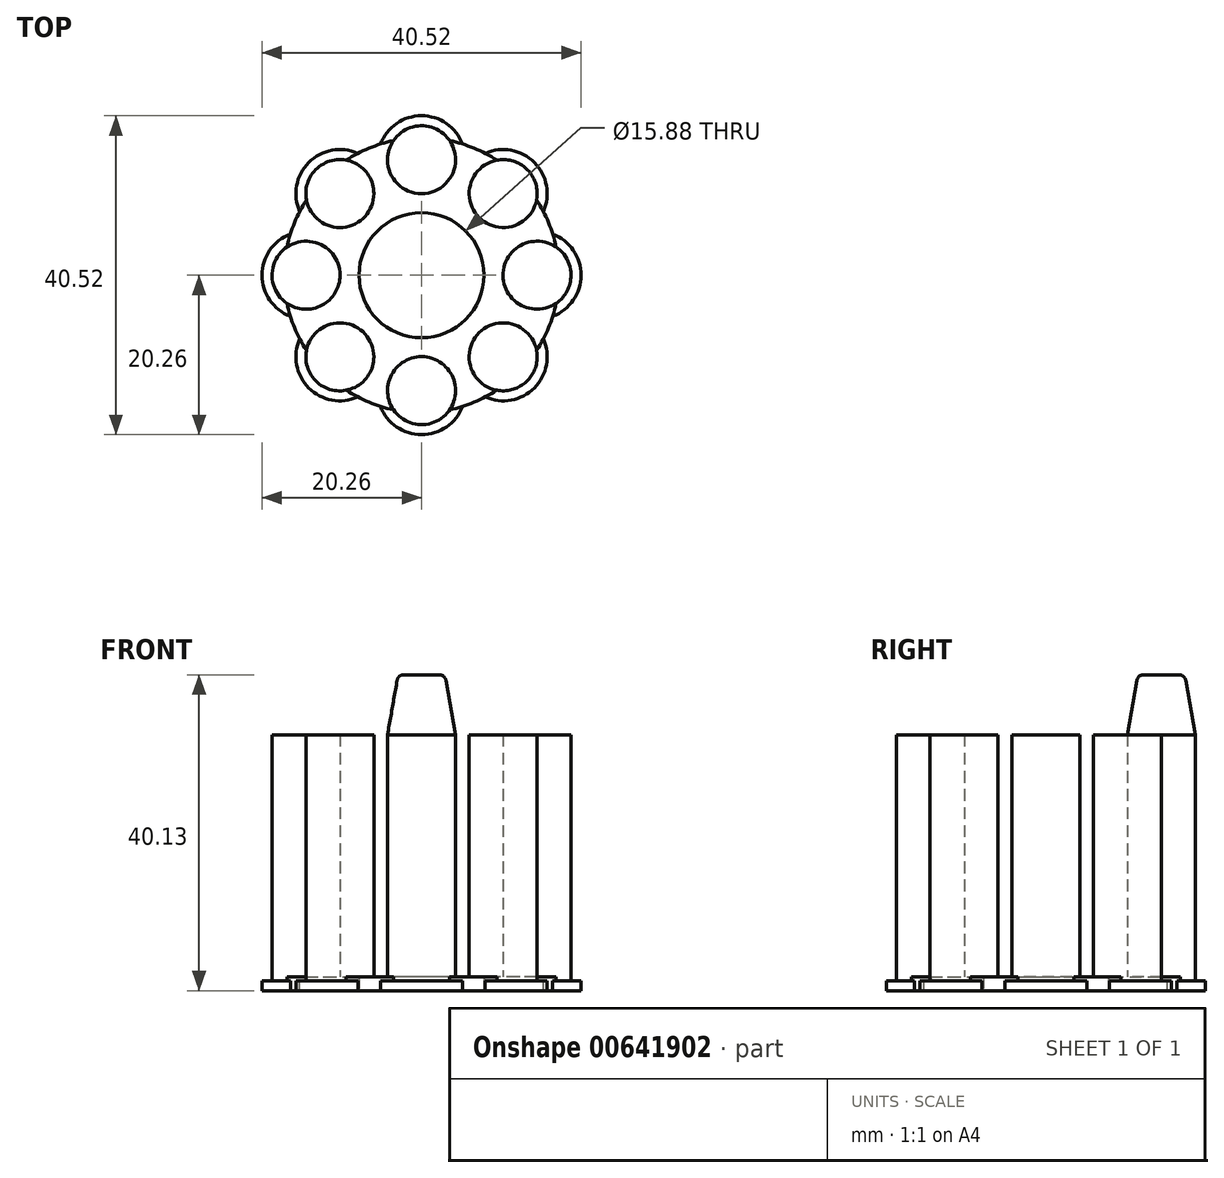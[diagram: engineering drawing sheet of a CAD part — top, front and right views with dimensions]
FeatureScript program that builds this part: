
annotation { "Feature Type Name" : "Feature", "Feature Type Description" : "" }
export const myFeature = defineFeature(function(context is Context, id is Id, definition is map)
    precondition{}
    {
        {
            var Q0;
            Q0=qCreatedBy(makeId("Top.planeOp"),FACE);
            var sketch = newSketch(context, id + "F0", { "sketchPlane" : qUnion([Q0])});
            skCircle(sketch, "E0", {"center": v(0, 14.67) * mm, "radius": 5.59 * mm});
            skCircle(sketch, "E1", {"center": v(0, 0) * mm, "radius": 7.94 * mm});
            skCircle(sketch, "E2", {"center": v(0, 14.67) * mm, "radius": 4.32 * mm});
            skCircle(sketch, "E3", {"center": v(0, 0) * mm, "radius": 17.46 * mm});
            skCircle(sketch, "E4.1.0", {"center": v(-10.37, 10.37) * mm, "radius": 4.32 * mm});
            skCircle(sketch, "E4.1.1", {"center": v(-10.37, 10.37) * mm, "radius": 5.59 * mm});
            skCircle(sketch, "E4.2.0", {"center": v(-14.67, 0) * mm, "radius": 4.32 * mm});
            skCircle(sketch, "E4.2.1", {"center": v(-14.67, 0) * mm, "radius": 5.59 * mm});
            skCircle(sketch, "E5.1.3.0", {"center": v(-10.37, -10.37) * mm, "radius": 4.32 * mm});
            skCircle(sketch, "E5.2.3.0", {"center": v(-10.37, -10.37) * mm, "radius": 5.59 * mm});
            skCircle(sketch, "E5.1.4.0", {"center": v(0, -14.67) * mm, "radius": 4.32 * mm});
            skCircle(sketch, "E5.2.4.0", {"center": v(0, -14.67) * mm, "radius": 5.59 * mm});
            skCircle(sketch, "E5.1.5.0", {"center": v(10.37, -10.37) * mm, "radius": 4.32 * mm});
            skCircle(sketch, "E5.2.5.0", {"center": v(10.37, -10.37) * mm, "radius": 5.59 * mm});
            skCircle(sketch, "E5.1.6.0", {"center": v(14.67, 0) * mm, "radius": 4.32 * mm});
            skCircle(sketch, "E5.2.6.0", {"center": v(14.67, 0) * mm, "radius": 5.59 * mm});
            skCircle(sketch, "E5.1.7.0", {"center": v(10.37, 10.37) * mm, "radius": 4.32 * mm});
            skCircle(sketch, "E5.2.7.0", {"center": v(10.37, 10.37) * mm, "radius": 5.59 * mm});
            skSolve(sketch);
        }
        {
            var Q0;
            {var subQ0=sQuery(id+"F0.wireOp",EDGE,"E3");var subQ1=sQuery(id+"F0.wireOp",EDGE,"E0");var subQ2=makeQuery(id+"F0.imprint","INTERSECT",VERTEX,{"disambiguationData":[OD(0.0)],"derivedFrom":[subQ1,subQ0]});Q0=makeQuery(id+"F0.imprint","IMPRINT",FACE,{"disambiguationData":[TD([[makeQuery(id+"F0.imprint","IMPRINT",EDGE,{"disambiguationData":[TD([[subQ2,1.0]])],"derivedFrom":subQ1}),1.0]])]});}
            var Q1;
            {var subQ0=sQuery(id+"F0.wireOp",EDGE,"E5.2.7.0");var subQ1=sQuery(id+"F0.wireOp",EDGE,"E3");var subQ2=makeQuery(id+"F0.imprint","INTERSECT",VERTEX,{"disambiguationData":[OD(0.0)],"derivedFrom":[subQ1,subQ0]});Q1=makeQuery(id+"F0.imprint","IMPRINT",FACE,{"disambiguationData":[TD([[makeQuery(id+"F0.imprint","IMPRINT",EDGE,{"disambiguationData":[TD([[subQ2,-1.0]])],"derivedFrom":subQ1}),1.0]])]});}
            var Q2;
            {var subQ0=sQuery(id+"F0.wireOp",EDGE,"E5.2.6.0");var subQ1=sQuery(id+"F0.wireOp",EDGE,"E3");var subQ2=makeQuery(id+"F0.imprint","INTERSECT",VERTEX,{"disambiguationData":[OD(0.0)],"derivedFrom":[subQ1,subQ0]});Q2=makeQuery(id+"F0.imprint","IMPRINT",FACE,{"disambiguationData":[TD([[makeQuery(id+"F0.imprint","IMPRINT",EDGE,{"disambiguationData":[TD([[subQ2,1.0]])],"derivedFrom":subQ1}),1.0]])]});}
            var Q3;
            {var subQ0=sQuery(id+"F0.wireOp",EDGE,"E5.2.5.0");var subQ1=sQuery(id+"F0.wireOp",EDGE,"E3");var subQ2=makeQuery(id+"F0.imprint","INTERSECT",VERTEX,{"disambiguationData":[OD(0.0)],"derivedFrom":[subQ1,subQ0]});Q3=makeQuery(id+"F0.imprint","IMPRINT",FACE,{"disambiguationData":[TD([[makeQuery(id+"F0.imprint","IMPRINT",EDGE,{"disambiguationData":[TD([[subQ2,-1.0]])],"derivedFrom":subQ1}),1.0]])]});}
            var Q4;
            {var subQ0=sQuery(id+"F0.wireOp",EDGE,"E5.2.4.0");var subQ1=sQuery(id+"F0.wireOp",EDGE,"E3");var subQ2=makeQuery(id+"F0.imprint","INTERSECT",VERTEX,{"disambiguationData":[OD(0.0)],"derivedFrom":[subQ1,subQ0]});Q4=makeQuery(id+"F0.imprint","IMPRINT",FACE,{"disambiguationData":[TD([[makeQuery(id+"F0.imprint","IMPRINT",EDGE,{"disambiguationData":[TD([[subQ2,-1.0]])],"derivedFrom":subQ1}),1.0]])]});}
            var Q5;
            {var subQ0=sQuery(id+"F0.wireOp",EDGE,"E5.2.3.0");var subQ1=sQuery(id+"F0.wireOp",EDGE,"E3");var subQ2=makeQuery(id+"F0.imprint","INTERSECT",VERTEX,{"disambiguationData":[OD(0.0)],"derivedFrom":[subQ1,subQ0]});Q5=makeQuery(id+"F0.imprint","IMPRINT",FACE,{"disambiguationData":[TD([[makeQuery(id+"F0.imprint","IMPRINT",EDGE,{"disambiguationData":[TD([[subQ2,-1.0]])],"derivedFrom":subQ1}),1.0]])]});}
            var Q6;
            {var subQ0=sQuery(id+"F0.wireOp",EDGE,"E4.2.1");var subQ1=sQuery(id+"F0.wireOp",EDGE,"E3");var subQ2=makeQuery(id+"F0.imprint","INTERSECT",VERTEX,{"disambiguationData":[OD(0.0)],"derivedFrom":[subQ1,subQ0]});Q6=makeQuery(id+"F0.imprint","IMPRINT",FACE,{"disambiguationData":[TD([[makeQuery(id+"F0.imprint","IMPRINT",EDGE,{"disambiguationData":[TD([[subQ2,-1.0]])],"derivedFrom":subQ1}),1.0]])]});}
            var Q7;
            {var subQ0=sQuery(id+"F0.wireOp",EDGE,"E4.1.1");var subQ1=sQuery(id+"F0.wireOp",EDGE,"E3");var subQ2=makeQuery(id+"F0.imprint","INTERSECT",VERTEX,{"disambiguationData":[OD(0.0)],"derivedFrom":[subQ1,subQ0]});Q7=makeQuery(id+"F0.imprint","IMPRINT",FACE,{"disambiguationData":[TD([[makeQuery(id+"F0.imprint","IMPRINT",EDGE,{"disambiguationData":[TD([[subQ2,-1.0]])],"derivedFrom":subQ1}),1.0]])]});}
            var Q8;
            Q8=makeQuery(id+"F0.imprint","IMPRINT",FACE,{"disambiguationData":[TD([[makeQuery(id+"F0.imprint","IMPRINT",EDGE,{"derivedFrom":sQuery(id+"F0.wireOp",EDGE,"E1")}),-1.0]])]});
            extrude(context, id + "F1", {"entities" : qUnion([Q0, Q1, Q2, Q3, Q4, Q5, Q6, Q7, Q8]), "depth" : 0.5 * mm, "offsetDistance" : 25.4 * mm});
        }
        {
            var Q0;
            Q0=qSketchRegion(id+"F0",true);
            var Q1;
            {var subQ0=sQuery(id+"F0.wireOp",EDGE,"E5.1.4.0");var subQ1=sQuery(id+"F0.wireOp",EDGE,"E3");var subQ2=makeQuery(id+"F0.imprint","INTERSECT",VERTEX,{"disambiguationData":[OD(0.0)],"derivedFrom":[subQ1,subQ0]});Q1=makeQuery(id+"F0.imprint","IMPRINT",FACE,{"disambiguationData":[TD([[makeQuery(id+"F0.imprint","IMPRINT",EDGE,{"disambiguationData":[TD([[subQ2,-1.0]])],"derivedFrom":subQ1}),-1.0]])]});}
            var Q2;
            {var subQ0=sQuery(id+"F0.wireOp",EDGE,"E5.1.4.0");var subQ1=sQuery(id+"F0.wireOp",EDGE,"E3");var subQ2=makeQuery(id+"F0.imprint","INTERSECT",VERTEX,{"disambiguationData":[OD(0.0)],"derivedFrom":[subQ1,subQ0]});Q2=makeQuery(id+"F0.imprint","IMPRINT",FACE,{"disambiguationData":[TD([[makeQuery(id+"F0.imprint","IMPRINT",EDGE,{"disambiguationData":[TD([[subQ2,-1.0]])],"derivedFrom":subQ1}),1.0]])]});}
            var Q3;
            {var subQ0=sQuery(id+"F0.wireOp",EDGE,"E5.1.5.0");var subQ1=sQuery(id+"F0.wireOp",EDGE,"E3");var subQ2=makeQuery(id+"F0.imprint","INTERSECT",VERTEX,{"disambiguationData":[OD(0.0)],"derivedFrom":[subQ1,subQ0]});Q3=makeQuery(id+"F0.imprint","IMPRINT",FACE,{"disambiguationData":[TD([[makeQuery(id+"F0.imprint","IMPRINT",EDGE,{"disambiguationData":[TD([[subQ2,-1.0]])],"derivedFrom":subQ1}),1.0]])]});}
            var Q4;
            {var subQ0=sQuery(id+"F0.wireOp",EDGE,"E5.1.5.0");var subQ1=sQuery(id+"F0.wireOp",EDGE,"E3");var subQ2=makeQuery(id+"F0.imprint","INTERSECT",VERTEX,{"disambiguationData":[OD(0.0)],"derivedFrom":[subQ1,subQ0]});Q4=makeQuery(id+"F0.imprint","IMPRINT",FACE,{"disambiguationData":[TD([[makeQuery(id+"F0.imprint","IMPRINT",EDGE,{"disambiguationData":[TD([[subQ2,-1.0]])],"derivedFrom":subQ1}),-1.0]])]});}
            var Q5;
            {var subQ0=sQuery(id+"F0.wireOp",EDGE,"E5.1.6.0");var subQ1=sQuery(id+"F0.wireOp",EDGE,"E3");var subQ2=makeQuery(id+"F0.imprint","INTERSECT",VERTEX,{"disambiguationData":[OD(0.0)],"derivedFrom":[subQ1,subQ0]});Q5=makeQuery(id+"F0.imprint","IMPRINT",FACE,{"disambiguationData":[TD([[makeQuery(id+"F0.imprint","IMPRINT",EDGE,{"disambiguationData":[TD([[subQ2,1.0]])],"derivedFrom":subQ1}),-1.0]])]});}
            var Q6;
            {var subQ0=sQuery(id+"F0.wireOp",EDGE,"E5.1.6.0");var subQ1=sQuery(id+"F0.wireOp",EDGE,"E3");var subQ2=makeQuery(id+"F0.imprint","INTERSECT",VERTEX,{"disambiguationData":[OD(0.0)],"derivedFrom":[subQ1,subQ0]});Q6=makeQuery(id+"F0.imprint","IMPRINT",FACE,{"disambiguationData":[TD([[makeQuery(id+"F0.imprint","IMPRINT",EDGE,{"disambiguationData":[TD([[subQ2,1.0]])],"derivedFrom":subQ1}),1.0]])]});}
            var Q7;
            {var subQ0=sQuery(id+"F0.wireOp",EDGE,"E5.1.7.0");var subQ1=sQuery(id+"F0.wireOp",EDGE,"E3");var subQ2=makeQuery(id+"F0.imprint","INTERSECT",VERTEX,{"disambiguationData":[OD(0.0)],"derivedFrom":[subQ1,subQ0]});Q7=makeQuery(id+"F0.imprint","IMPRINT",FACE,{"disambiguationData":[TD([[makeQuery(id+"F0.imprint","IMPRINT",EDGE,{"disambiguationData":[TD([[subQ2,-1.0]])],"derivedFrom":subQ1}),1.0]])]});}
            var Q8;
            {var subQ0=sQuery(id+"F0.wireOp",EDGE,"E5.1.7.0");var subQ1=sQuery(id+"F0.wireOp",EDGE,"E3");var subQ2=makeQuery(id+"F0.imprint","INTERSECT",VERTEX,{"disambiguationData":[OD(0.0)],"derivedFrom":[subQ1,subQ0]});Q8=makeQuery(id+"F0.imprint","IMPRINT",FACE,{"disambiguationData":[TD([[makeQuery(id+"F0.imprint","IMPRINT",EDGE,{"disambiguationData":[TD([[subQ2,-1.0]])],"derivedFrom":subQ1}),-1.0]])]});}
            var Q9;
            {var subQ0=sQuery(id+"F0.wireOp",EDGE,"E4.1.0");var subQ1=sQuery(id+"F0.wireOp",EDGE,"E3");var subQ2=makeQuery(id+"F0.imprint","INTERSECT",VERTEX,{"disambiguationData":[OD(0.0)],"derivedFrom":[subQ1,subQ0]});Q9=makeQuery(id+"F0.imprint","IMPRINT",FACE,{"disambiguationData":[TD([[makeQuery(id+"F0.imprint","IMPRINT",EDGE,{"disambiguationData":[TD([[subQ2,-1.0]])],"derivedFrom":subQ1}),1.0]])]});}
            var Q10;
            {var subQ0=sQuery(id+"F0.wireOp",EDGE,"E4.1.0");var subQ1=sQuery(id+"F0.wireOp",EDGE,"E3");var subQ2=makeQuery(id+"F0.imprint","INTERSECT",VERTEX,{"disambiguationData":[OD(0.0)],"derivedFrom":[subQ1,subQ0]});Q10=makeQuery(id+"F0.imprint","IMPRINT",FACE,{"disambiguationData":[TD([[makeQuery(id+"F0.imprint","IMPRINT",EDGE,{"disambiguationData":[TD([[subQ2,-1.0]])],"derivedFrom":subQ1}),-1.0]])]});}
            var Q11;
            {var subQ0=sQuery(id+"F0.wireOp",EDGE,"E4.2.0");var subQ1=sQuery(id+"F0.wireOp",EDGE,"E3");var subQ2=makeQuery(id+"F0.imprint","INTERSECT",VERTEX,{"disambiguationData":[OD(0.0)],"derivedFrom":[subQ1,subQ0]});Q11=makeQuery(id+"F0.imprint","IMPRINT",FACE,{"disambiguationData":[TD([[makeQuery(id+"F0.imprint","IMPRINT",EDGE,{"disambiguationData":[TD([[subQ2,-1.0]])],"derivedFrom":subQ1}),1.0]])]});}
            var Q12;
            {var subQ0=sQuery(id+"F0.wireOp",EDGE,"E3");var subQ1=sQuery(id+"F0.wireOp",EDGE,"E2");var subQ2=makeQuery(id+"F0.imprint","INTERSECT",VERTEX,{"disambiguationData":[OD(0.0)],"derivedFrom":[subQ1,subQ0]});Q12=makeQuery(id+"F0.imprint","IMPRINT",FACE,{"disambiguationData":[TD([[makeQuery(id+"F0.imprint","IMPRINT",EDGE,{"disambiguationData":[TD([[subQ2,1.0]])],"derivedFrom":subQ1}),1.0]])]});}
            var Q13;
            {var subQ0=sQuery(id+"F0.wireOp",EDGE,"E3");var subQ1=sQuery(id+"F0.wireOp",EDGE,"E2");var subQ2=makeQuery(id+"F0.imprint","INTERSECT",VERTEX,{"disambiguationData":[OD(0.0)],"derivedFrom":[subQ1,subQ0]});Q13=makeQuery(id+"F0.imprint","IMPRINT",FACE,{"disambiguationData":[TD([[makeQuery(id+"F0.imprint","IMPRINT",EDGE,{"disambiguationData":[TD([[subQ2,-1.0]])],"derivedFrom":subQ1}),1.0]])]});}
            var Q14;
            {var subQ0=sQuery(id+"F0.wireOp",EDGE,"E5.1.3.0");var subQ1=sQuery(id+"F0.wireOp",EDGE,"E3");var subQ2=makeQuery(id+"F0.imprint","INTERSECT",VERTEX,{"disambiguationData":[OD(0.0)],"derivedFrom":[subQ1,subQ0]});Q14=makeQuery(id+"F0.imprint","IMPRINT",FACE,{"disambiguationData":[TD([[makeQuery(id+"F0.imprint","IMPRINT",EDGE,{"disambiguationData":[TD([[subQ2,-1.0]])],"derivedFrom":subQ1}),-1.0]])]});}
            var Q15;
            {var subQ0=sQuery(id+"F0.wireOp",EDGE,"E5.1.3.0");var subQ1=sQuery(id+"F0.wireOp",EDGE,"E3");var subQ2=makeQuery(id+"F0.imprint","INTERSECT",VERTEX,{"disambiguationData":[OD(0.0)],"derivedFrom":[subQ1,subQ0]});Q15=makeQuery(id+"F0.imprint","IMPRINT",FACE,{"disambiguationData":[TD([[makeQuery(id+"F0.imprint","IMPRINT",EDGE,{"disambiguationData":[TD([[subQ2,-1.0]])],"derivedFrom":subQ1}),1.0]])]});}
            var Q16;
            {var subQ0=sQuery(id+"F0.wireOp",EDGE,"E4.2.0");var subQ1=sQuery(id+"F0.wireOp",EDGE,"E3");var subQ2=makeQuery(id+"F0.imprint","INTERSECT",VERTEX,{"disambiguationData":[OD(0.0)],"derivedFrom":[subQ1,subQ0]});Q16=makeQuery(id+"F0.imprint","IMPRINT",FACE,{"disambiguationData":[TD([[makeQuery(id+"F0.imprint","IMPRINT",EDGE,{"disambiguationData":[TD([[subQ2,-1.0]])],"derivedFrom":subQ1}),-1.0]])]});}
            extrude(context, id + "F2", {"entities" : qUnion([Q0, Q1, Q2, Q3, Q4, Q5, Q6, Q7, Q8, Q9, Q10, Q11, Q12, Q13, Q14, Q15, Q16]), "operationType" : NewBodyOperationType.ADD, "oppositeDirection" : true, "depth" : 1.27 * mm, "offsetDistance" : 25.4 * mm});
        }
        {
            var Q0;
            {var subQ0=sQuery(id+"F0.wireOp",EDGE,"E5.1.5.0");var subQ1=sQuery(id+"F0.wireOp",EDGE,"E3");var subQ2=makeQuery(id+"F0.imprint","INTERSECT",VERTEX,{"disambiguationData":[OD(0.0)],"derivedFrom":[subQ1,subQ0]});Q0=makeQuery(id+"F0.imprint","IMPRINT",FACE,{"disambiguationData":[TD([[makeQuery(id+"F0.imprint","IMPRINT",EDGE,{"disambiguationData":[TD([[subQ2,-1.0]])],"derivedFrom":subQ1}),1.0]])]});}
            var Q1;
            {var subQ0=sQuery(id+"F0.wireOp",EDGE,"E5.1.5.0");var subQ1=sQuery(id+"F0.wireOp",EDGE,"E3");var subQ2=makeQuery(id+"F0.imprint","INTERSECT",VERTEX,{"disambiguationData":[OD(0.0)],"derivedFrom":[subQ1,subQ0]});Q1=makeQuery(id+"F0.imprint","IMPRINT",FACE,{"disambiguationData":[TD([[makeQuery(id+"F0.imprint","IMPRINT",EDGE,{"disambiguationData":[TD([[subQ2,-1.0]])],"derivedFrom":subQ1}),-1.0]])]});}
            var Q2;
            {var subQ0=sQuery(id+"F0.wireOp",EDGE,"E5.1.4.0");var subQ1=sQuery(id+"F0.wireOp",EDGE,"E3");var subQ2=makeQuery(id+"F0.imprint","INTERSECT",VERTEX,{"disambiguationData":[OD(0.0)],"derivedFrom":[subQ1,subQ0]});Q2=makeQuery(id+"F0.imprint","IMPRINT",FACE,{"disambiguationData":[TD([[makeQuery(id+"F0.imprint","IMPRINT",EDGE,{"disambiguationData":[TD([[subQ2,-1.0]])],"derivedFrom":subQ1}),-1.0]])]});}
            var Q3;
            {var subQ0=sQuery(id+"F0.wireOp",EDGE,"E5.1.4.0");var subQ1=sQuery(id+"F0.wireOp",EDGE,"E3");var subQ2=makeQuery(id+"F0.imprint","INTERSECT",VERTEX,{"disambiguationData":[OD(0.0)],"derivedFrom":[subQ1,subQ0]});Q3=makeQuery(id+"F0.imprint","IMPRINT",FACE,{"disambiguationData":[TD([[makeQuery(id+"F0.imprint","IMPRINT",EDGE,{"disambiguationData":[TD([[subQ2,-1.0]])],"derivedFrom":subQ1}),1.0]])]});}
            var Q4;
            {var subQ0=sQuery(id+"F0.wireOp",EDGE,"E5.1.3.0");var subQ1=sQuery(id+"F0.wireOp",EDGE,"E3");var subQ2=makeQuery(id+"F0.imprint","INTERSECT",VERTEX,{"disambiguationData":[OD(0.0)],"derivedFrom":[subQ1,subQ0]});Q4=makeQuery(id+"F0.imprint","IMPRINT",FACE,{"disambiguationData":[TD([[makeQuery(id+"F0.imprint","IMPRINT",EDGE,{"disambiguationData":[TD([[subQ2,-1.0]])],"derivedFrom":subQ1}),1.0]])]});}
            var Q5;
            {var subQ0=sQuery(id+"F0.wireOp",EDGE,"E5.1.3.0");var subQ1=sQuery(id+"F0.wireOp",EDGE,"E3");var subQ2=makeQuery(id+"F0.imprint","INTERSECT",VERTEX,{"disambiguationData":[OD(0.0)],"derivedFrom":[subQ1,subQ0]});Q5=makeQuery(id+"F0.imprint","IMPRINT",FACE,{"disambiguationData":[TD([[makeQuery(id+"F0.imprint","IMPRINT",EDGE,{"disambiguationData":[TD([[subQ2,-1.0]])],"derivedFrom":subQ1}),-1.0]])]});}
            var Q6;
            {var subQ0=sQuery(id+"F0.wireOp",EDGE,"E4.2.0");var subQ1=sQuery(id+"F0.wireOp",EDGE,"E3");var subQ2=makeQuery(id+"F0.imprint","INTERSECT",VERTEX,{"disambiguationData":[OD(0.0)],"derivedFrom":[subQ1,subQ0]});Q6=makeQuery(id+"F0.imprint","IMPRINT",FACE,{"disambiguationData":[TD([[makeQuery(id+"F0.imprint","IMPRINT",EDGE,{"disambiguationData":[TD([[subQ2,-1.0]])],"derivedFrom":subQ1}),1.0]])]});}
            var Q7;
            {var subQ0=sQuery(id+"F0.wireOp",EDGE,"E4.2.0");var subQ1=sQuery(id+"F0.wireOp",EDGE,"E3");var subQ2=makeQuery(id+"F0.imprint","INTERSECT",VERTEX,{"disambiguationData":[OD(0.0)],"derivedFrom":[subQ1,subQ0]});Q7=makeQuery(id+"F0.imprint","IMPRINT",FACE,{"disambiguationData":[TD([[makeQuery(id+"F0.imprint","IMPRINT",EDGE,{"disambiguationData":[TD([[subQ2,-1.0]])],"derivedFrom":subQ1}),-1.0]])]});}
            var Q8;
            {var subQ0=sQuery(id+"F0.wireOp",EDGE,"E4.1.0");var subQ1=sQuery(id+"F0.wireOp",EDGE,"E3");var subQ2=makeQuery(id+"F0.imprint","INTERSECT",VERTEX,{"disambiguationData":[OD(0.0)],"derivedFrom":[subQ1,subQ0]});Q8=makeQuery(id+"F0.imprint","IMPRINT",FACE,{"disambiguationData":[TD([[makeQuery(id+"F0.imprint","IMPRINT",EDGE,{"disambiguationData":[TD([[subQ2,-1.0]])],"derivedFrom":subQ1}),1.0]])]});}
            var Q9;
            {var subQ0=sQuery(id+"F0.wireOp",EDGE,"E4.1.0");var subQ1=sQuery(id+"F0.wireOp",EDGE,"E3");var subQ2=makeQuery(id+"F0.imprint","INTERSECT",VERTEX,{"disambiguationData":[OD(0.0)],"derivedFrom":[subQ1,subQ0]});Q9=makeQuery(id+"F0.imprint","IMPRINT",FACE,{"disambiguationData":[TD([[makeQuery(id+"F0.imprint","IMPRINT",EDGE,{"disambiguationData":[TD([[subQ2,-1.0]])],"derivedFrom":subQ1}),-1.0]])]});}
            var Q10;
            {var subQ0=sQuery(id+"F0.wireOp",EDGE,"E3");var subQ1=sQuery(id+"F0.wireOp",EDGE,"E2");var subQ2=makeQuery(id+"F0.imprint","INTERSECT",VERTEX,{"disambiguationData":[OD(0.0)],"derivedFrom":[subQ1,subQ0]});Q10=makeQuery(id+"F0.imprint","IMPRINT",FACE,{"disambiguationData":[TD([[makeQuery(id+"F0.imprint","IMPRINT",EDGE,{"disambiguationData":[TD([[subQ2,1.0]])],"derivedFrom":subQ1}),1.0]])]});}
            var Q11;
            {var subQ0=sQuery(id+"F0.wireOp",EDGE,"E3");var subQ1=sQuery(id+"F0.wireOp",EDGE,"E2");var subQ2=makeQuery(id+"F0.imprint","INTERSECT",VERTEX,{"disambiguationData":[OD(0.0)],"derivedFrom":[subQ1,subQ0]});Q11=makeQuery(id+"F0.imprint","IMPRINT",FACE,{"disambiguationData":[TD([[makeQuery(id+"F0.imprint","IMPRINT",EDGE,{"disambiguationData":[TD([[subQ2,-1.0]])],"derivedFrom":subQ1}),1.0]])]});}
            var Q12;
            {var subQ0=sQuery(id+"F0.wireOp",EDGE,"E5.1.7.0");var subQ1=sQuery(id+"F0.wireOp",EDGE,"E3");var subQ2=makeQuery(id+"F0.imprint","INTERSECT",VERTEX,{"disambiguationData":[OD(0.0)],"derivedFrom":[subQ1,subQ0]});Q12=makeQuery(id+"F0.imprint","IMPRINT",FACE,{"disambiguationData":[TD([[makeQuery(id+"F0.imprint","IMPRINT",EDGE,{"disambiguationData":[TD([[subQ2,-1.0]])],"derivedFrom":subQ1}),1.0]])]});}
            var Q13;
            {var subQ0=sQuery(id+"F0.wireOp",EDGE,"E5.1.7.0");var subQ1=sQuery(id+"F0.wireOp",EDGE,"E3");var subQ2=makeQuery(id+"F0.imprint","INTERSECT",VERTEX,{"disambiguationData":[OD(0.0)],"derivedFrom":[subQ1,subQ0]});Q13=makeQuery(id+"F0.imprint","IMPRINT",FACE,{"disambiguationData":[TD([[makeQuery(id+"F0.imprint","IMPRINT",EDGE,{"disambiguationData":[TD([[subQ2,-1.0]])],"derivedFrom":subQ1}),-1.0]])]});}
            var Q14;
            {var subQ0=sQuery(id+"F0.wireOp",EDGE,"E5.1.6.0");var subQ1=sQuery(id+"F0.wireOp",EDGE,"E3");var subQ2=makeQuery(id+"F0.imprint","INTERSECT",VERTEX,{"disambiguationData":[OD(0.0)],"derivedFrom":[subQ1,subQ0]});Q14=makeQuery(id+"F0.imprint","IMPRINT",FACE,{"disambiguationData":[TD([[makeQuery(id+"F0.imprint","IMPRINT",EDGE,{"disambiguationData":[TD([[subQ2,1.0]])],"derivedFrom":subQ1}),1.0]])]});}
            var Q15;
            {var subQ0=sQuery(id+"F0.wireOp",EDGE,"E5.1.6.0");var subQ1=sQuery(id+"F0.wireOp",EDGE,"E3");var subQ2=makeQuery(id+"F0.imprint","INTERSECT",VERTEX,{"disambiguationData":[OD(0.0)],"derivedFrom":[subQ1,subQ0]});Q15=makeQuery(id+"F0.imprint","IMPRINT",FACE,{"disambiguationData":[TD([[makeQuery(id+"F0.imprint","IMPRINT",EDGE,{"disambiguationData":[TD([[subQ2,1.0]])],"derivedFrom":subQ1}),-1.0]])]});}
            extrude(context, id + "F3", {"entities" : qUnion([Q0, Q1, Q2, Q3, Q4, Q5, Q6, Q7, Q8, Q9, Q10, Q11, Q12, Q13, Q14, Q15]), "operationType" : NewBodyOperationType.ADD, "depth" : 31.24 * mm, "offsetDistance" : 25.4 * mm});
        }
        {
            var Q0;
            Q0=qCreatedBy(makeId("Right.planeOp"),FACE);
            var sketch = newSketch(context, id + "F4", { "sketchPlane" : qUnion([Q0])});
            skLineSegment(sketch, "E6", {"start": v(14.67, 31.24) * mm, "end": v(14.67, 38.86) * mm});
            skLineSegment(sketch, "E7", {"start": v(18.99, 31.24) * mm, "end": v(14.67, 31.24) * mm});
            skLineSegment(sketch, "E8", {"start": v(0, 0) * mm, "end": v(0, 29.34) * mm, "construction": true});
            skLineSegment(sketch, "E9", {"start": v(18.99, 31.24) * mm, "end": v(17.77, 38.16) * mm});
            skLineSegment(sketch, "E10", {"start": v(14.67, 38.86) * mm, "end": v(16.93, 38.86) * mm});
            skPoint(sketch, "E11.visualSharp", {"position": v(17.64, 38.86) * mm});
            skArc(sketch, "E11.filletArc", {"start": v(17.77, 38.16) * mm, "mid": v(17.48, 38.66) * mm, "end": v(16.93, 38.86) * mm});
            skLineSegment(sketch, "E12", {"start": v(25.4, -1.27) * mm, "end": v(25.4, 38.86) * mm, "construction": true});
            skSolve(sketch);
        }
        {
            var Q0;
            Q0=makeQuery(id+"F4.imprint","IMPRINT",FACE,{"disambiguationData":[TD([[makeQuery(id+"F4.imprint","IMPRINT",EDGE,{"derivedFrom":sQuery(id+"F4.wireOp",EDGE,"E6")}),-1.0]])]});
            var Q1;
            Q1=sQuery(id+"F4.wireOp",EDGE,"E6");
            revolve(context, id + "F5", {"operationType" : NewBodyOperationType.ADD, "entities" : qUnion([Q0]), "axis" : qUnion([Q1]), "revolveType" : RevolveType.FULL});
        }
    });
